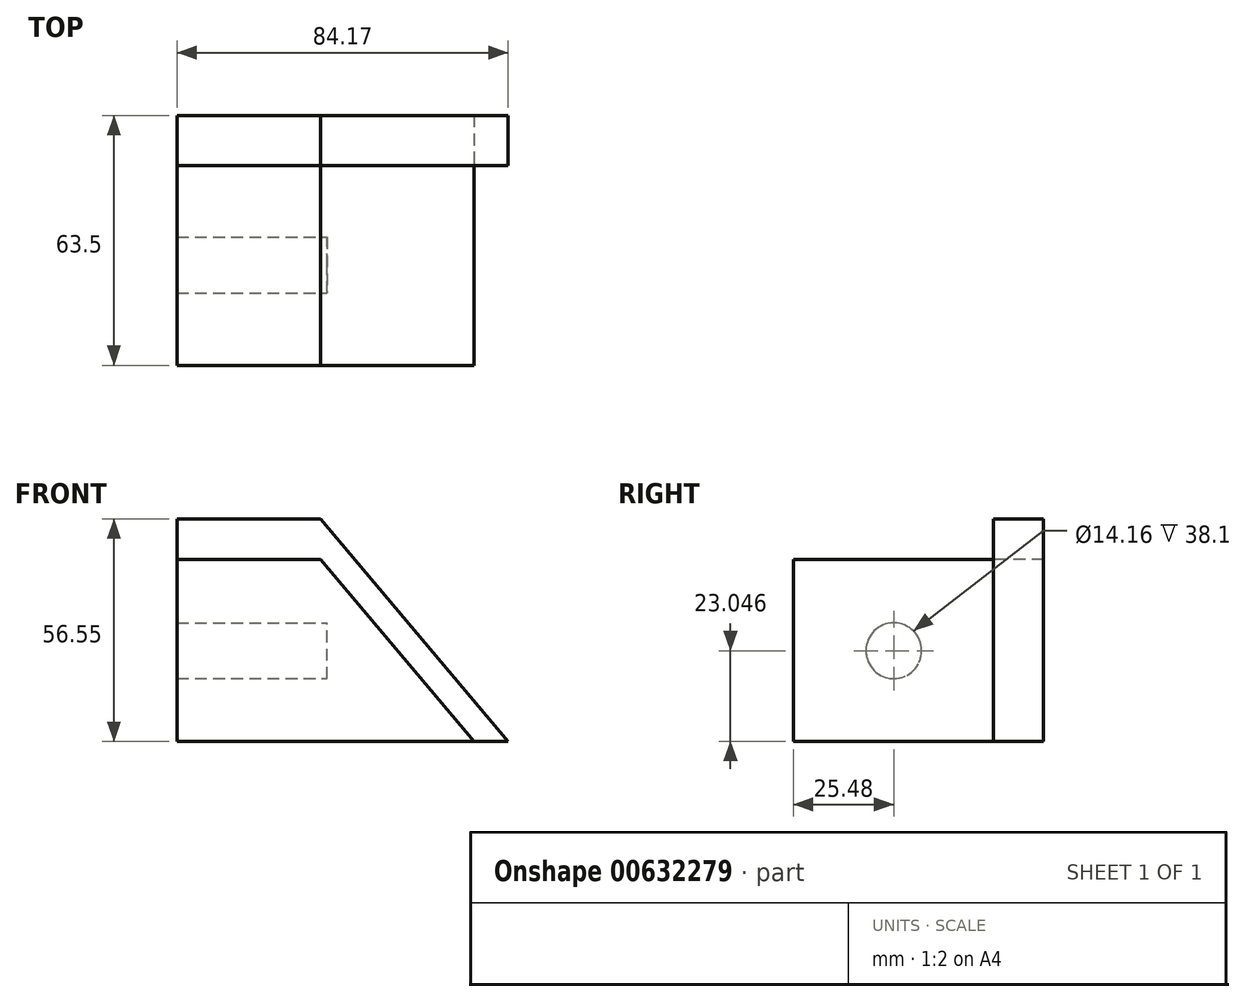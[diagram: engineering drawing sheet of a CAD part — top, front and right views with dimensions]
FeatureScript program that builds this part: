
annotation { "Feature Type Name" : "Feature", "Feature Type Description" : "" }
export const myFeature = defineFeature(function(context is Context, id is Id, definition is map)
    precondition{}
    {
        {
            var Q0;
            Q0=qCreatedBy(makeId("Front.planeOp"),FACE);
            var sketch = newSketch(context, id + "F0", { "sketchPlane" : qUnion([Q0])});
            skLineSegment(sketch, "E0", {"start": v(0, 0) * mm, "end": v(0, 56.55) * mm});
            skLineSegment(sketch, "E1", {"start": v(0, 56.55) * mm, "end": v(36.54, 56.55) * mm});
            skLineSegment(sketch, "E2", {"start": v(36.54, 56.55) * mm, "end": v(84.17, 0) * mm});
            skLineSegment(sketch, "E3", {"start": v(84.17, 0) * mm, "end": v(0, 0) * mm});
            skLineSegment(sketch, "E4", {"start": v(0, 46.3) * mm, "end": v(36.54, 46.3) * mm});
            skLineSegment(sketch, "E5", {"start": v(36.54, 46.3) * mm, "end": v(75.53, 0) * mm});
            skSolve(sketch);
        }
        {
            var Q0;
            {var subQ3=sQuery(id+"F0.wireOp",EDGE,"E4");Q0=makeQuery(id+"F0.imprint","IMPRINT",FACE,{"disambiguationData":[TD([[makeQuery(id+"F0.imprint","IMPRINT",EDGE,{"derivedFrom":subQ3}),-1.0]])]});}
            extrude(context, id + "F1", {"entities" : qUnion([Q0]), "depth" : 50.8 * mm, "offsetDistance" : 25.4 * mm});
        }
        {
            var Q0;
            {var subQ3=sQuery(id+"F0.wireOp",EDGE,"E1");Q0=makeQuery(id+"F0.imprint","IMPRINT",FACE,{"disambiguationData":[TD([[makeQuery(id+"F0.imprint","IMPRINT",EDGE,{"derivedFrom":subQ3}),-1.0]])]});}
            extrude(context, id + "F2", {"entities" : qUnion([Q0]), "oppositeDirection" : true, "depth" : 12.7 * mm, "offsetDistance" : 25.4 * mm});
        }
        {
            var Q0;
            Q0=qCreatedBy(makeId("Right.planeOp"),FACE);
            var sketch = newSketch(context, id + "F3", { "sketchPlane" : qUnion([Q0])});
            skCircle(sketch, "E6", {"center": v(-25.32, 23.05) * mm, "radius": 7.08 * mm});
            skSolve(sketch);
        }
        {
            var Q0;
            Q0 = qSketchRegion(id + "F3", true);
            extrude(context, id + "F4", {"entities" : qUnion([Q0]), "operationType" : NewBodyOperationType.REMOVE, "endBound" : BoundingType.SYMMETRIC, "oppositeDirection" : true, "depth" : 76.2 * mm, "offsetDistance" : 25.4 * mm});
        }
    });
